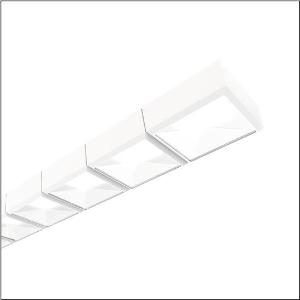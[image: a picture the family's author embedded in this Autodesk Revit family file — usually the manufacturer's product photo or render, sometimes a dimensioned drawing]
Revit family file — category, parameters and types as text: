
# Revit family: scriptus_r__11_5mz314d04wa_e059
name_source: partatom
category: Lighting Fixtures
units: mm (PartAtom-declared; Revit-internal decimal feet)

## family parameters
Cut with Voids When Loaded = No
Host = Face
Light Source = No
Part Type = Normal
Room Calculation Point = No
Round Connector Dimension = Use Diameter
Shared = No

## types (1)
- Scriptus® 11 (1 x LED 4000K / CRI = 80 (unbekannt), 3220 lm / 4820 lm, 4000K)
    Apparent Load = 120 VA
    CIE Flux Codes = - - - 0 100 / 82 95 99 100 100
    Color Rendering = 80
    Color Temperature = 4000K
    Default Elevation = 1800 mm
    Description = Scriptus® 11, office luminaire, primary optical cover: lenses, CAT 2 (L<= 3000cd/m²), light emission: direct/indirect distribution, primary light characteristic: symmetric, installation type: suspended mounting, LED, rated luminous flux: 16.060lm, luminous efficacy: 133lm/W, light colour: 840, colour temperature: 4000K, control gear: ECG DALI, with terminal, 5-pole, mains connection: 230V, AC, 50Hz, rated input power: 120W, LED, control gear: ECG DALI, housing, luminaire housing, of aluminium, traffic white (RAL 9016), length: 3.088mm, width: 114mm, height: 57mm, protection rating (complete): IP20, insulation class (complete): insulation class I (protective earthing), certification: CE, ENEC, VDE, protection symbol: F, permissible operating ambient temperature: 0..+35°C, standard: EN 50419, packaging unit: 1 piece
    Height = 57 mm
    Lamp = 1 x LED 4000K / CRI >= 80 (unbekannt)
    Lamp Light Flux = 3220 lm / 4820 lm
    Lamp count = 1
    Length = 3088 mm
    Luminous efficacy = 134 lm/W
    Manufacturer = Siteco
    ModVariant = No
    Model = 5MZ314D04WA
    Mounting Place = Ceiling
    Mounting Type = Pendant
    Number of Poles = 1
    OnlyDefault = Yes
    Power Factor = 1
    Product Name = Scriptus® 11
    Product group = office luminaire | ceiling pendant
    ProductGroupID = 902
    Protection Class = Protection class I
    Protection Degree = IP 20
    RLX_Detail_Level = 1
    RLX_Emergency_Light_Flux = 0 lm
    RLX_Emergency_Type = 0
    RLX_Emergency_Type_DB = No
    RlxData = <blob elided: 31977 chars, md5=d9ac50c4>
    Socket = socket
    Standby Power = 0 W
    System Light Flux = 16080 lm
    System Power = 120 W
    Type Comments = Product without accessories
    Type Image = l_1004839.jpg
    URL = http://relux.com
    VarID = ---
    Voltage = 0 V
    Weight = 0.00 kg
    Width = 114 mm

## geometry (parser evidence)
native form markers: Blend x4, Sweep x21
no freeform markers — native parametric forms only
